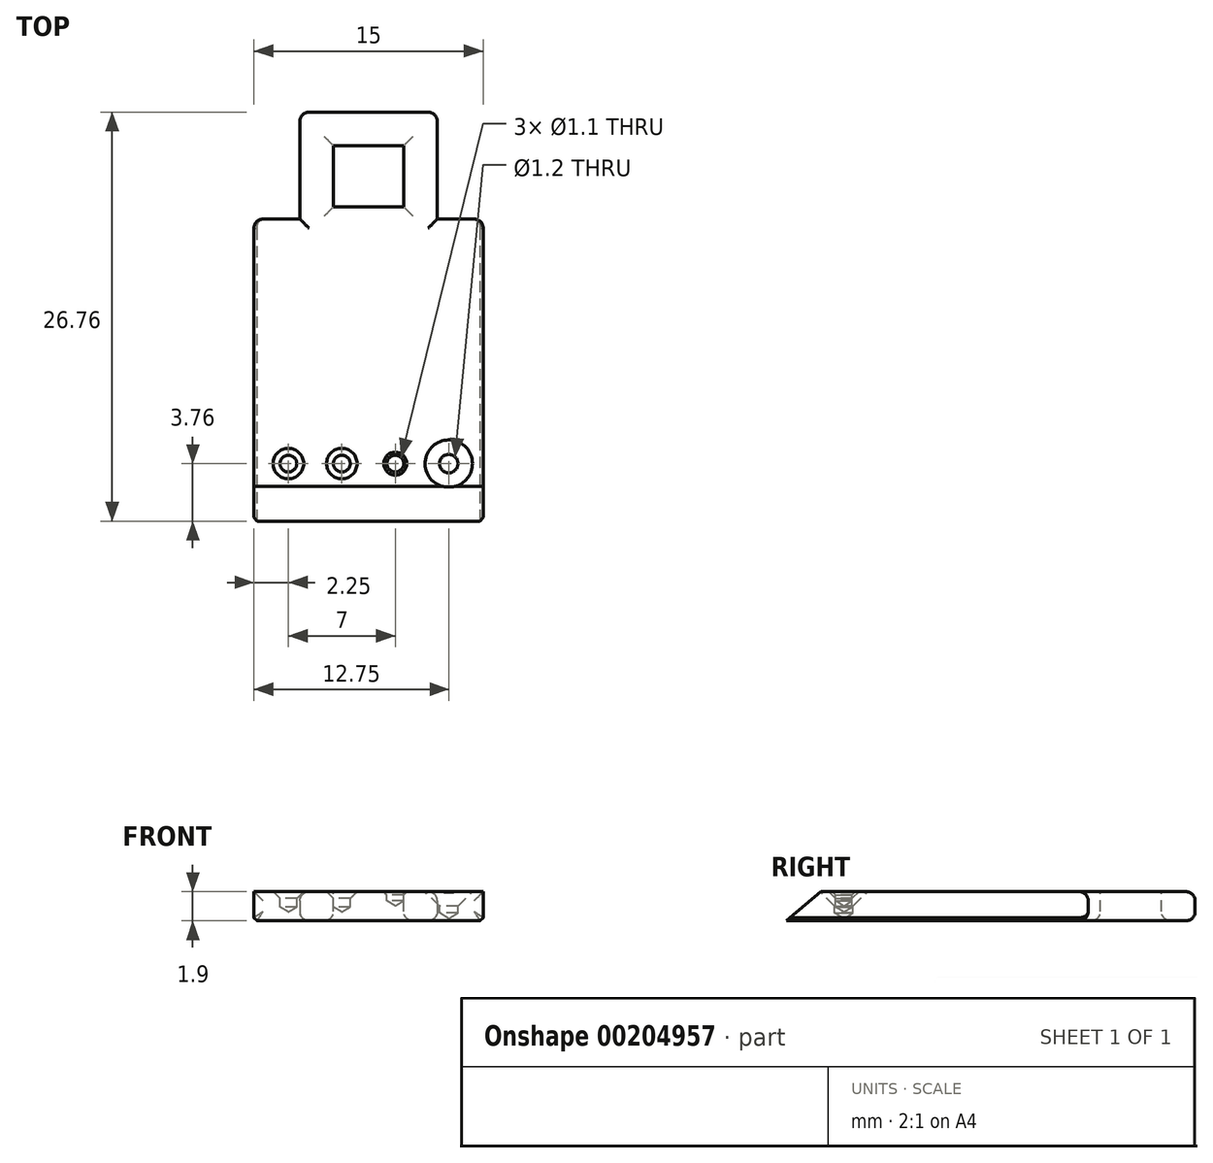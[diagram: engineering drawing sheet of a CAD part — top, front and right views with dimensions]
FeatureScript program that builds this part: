
annotation { "Feature Type Name" : "Feature", "Feature Type Description" : "" }
export const myFeature = defineFeature(function(context is Context, id is Id, definition is map)
    precondition{}
    {
        {
            var Q0;
            Q0=qCreatedBy(makeId("Top.planeOp"),FACE);
            var sketch = newSketch(context, id + "F0", { "sketchPlane" : qUnion([Q0])});
            skLineSegment(sketch, "E0.bottom", {"start": v(-7.5, 0) * mm, "end": v(7.5, 0) * mm});
            skLineSegment(sketch, "E0.top", {"start": v(-7.5, 20) * mm, "end": v(7.5, 20) * mm});
            skLineSegment(sketch, "E0.left", {"start": v(-7.5, 0) * mm, "end": v(-7.5, 20) * mm});
            skLineSegment(sketch, "E0.right", {"start": v(7.5, 0) * mm, "end": v(7.5, 20) * mm});
            skSolve(sketch);
        }
        {
            var Q0;
            Q0 = qSketchRegion(id + "F0", true);
            extrude(context, id + "F1", {"entities" : qUnion([Q0]), "depth" : 1.9 * mm});
        }
        {
            var Q0;
            Q0=makeQuery(id+"F1.opExtrude","CAP_FACE",FACE,{"disambiguationData":[OSD([sQuery(id+"F0.wireOp",EDGE,"E0.bottom"),sQuery(id+"F0.wireOp",EDGE,"E0.top"),sQuery(id+"F0.wireOp",EDGE,"E0.left"),sQuery(id+"F0.wireOp",EDGE,"E0.right")])],"isStart":false});
            var sketch = newSketch(context, id + "F2", { "sketchPlane" : qUnion([Q0])});
            skLineSegment(sketch, "E1", {"start": v(-7.5, 4) * mm, "end": v(7.5, 4) * mm, "construction": true});
            skPoint(sketch, "E2", {"position": v(-5.25, 4) * mm});
            skPoint(sketch, "E3", {"position": v(-1.75, 4) * mm});
            skPoint(sketch, "E4", {"position": v(1.75, 4) * mm});
            skPoint(sketch, "E5", {"position": v(5.25, 4) * mm});
            skSolve(sketch);
        }
        {
            var Q0;
            Q0=sQuery(id+"F2.wireOp",VERTEX,"E2");
            var Q1;
            Q1=sQuery(id+"F2.wireOp",VERTEX,"E3");
            var Q2;
            Q2=makeQuery(id+"F1.opExtrude","SWEPT_BODY",BODY,{"disambiguationData":[OSD([sQuery(id+"F0.wireOp",EDGE,"E0.bottom"),sQuery(id+"F0.wireOp",EDGE,"E0.top"),sQuery(id+"F0.wireOp",EDGE,"E0.left"),sQuery(id+"F0.wireOp",EDGE,"E0.right")])]});
            hole(context, id + "F3", {"style" : HoleStyle.C_SINK, "endStyle" : HoleEndStyle.BLIND, "holeDiameter" : 1.1 * mm, "cSinkDiameter" : 2 * mm, "cSinkAngle" : 90 * degree, "holeDepth" : 1 * mm, "locations" : qUnion([Q0, Q1]), "scope" : qUnion([Q2])});
        }
        {
            var Q0;
            Q0=sQuery(id+"F2.wireOp",VERTEX,"E4");
            var Q1;
            Q1=makeQuery(id+"F1.opExtrude","SWEPT_BODY",BODY,{"disambiguationData":[OSD([sQuery(id+"F0.wireOp",EDGE,"E0.bottom"),sQuery(id+"F0.wireOp",EDGE,"E0.top"),sQuery(id+"F0.wireOp",EDGE,"E0.left"),sQuery(id+"F0.wireOp",EDGE,"E0.right")])]});
            hole(context, id + "F4", {"style" : HoleStyle.C_SINK, "endStyle" : HoleEndStyle.BLIND, "holeDiameter" : 1.1 * mm, "cSinkDiameter" : 1.5 * mm, "cSinkAngle" : 90 * degree, "holeDepth" : .6 * mm, "locations" : qUnion([Q0]), "scope" : qUnion([Q1])});
        }
        {
            var Q0;
            Q0=sQuery(id+"F2.wireOp",VERTEX,"E5");
            var Q1;
            Q1=makeQuery(id+"F1.opExtrude","SWEPT_BODY",BODY,{"disambiguationData":[OSD([sQuery(id+"F0.wireOp",EDGE,"E0.bottom"),sQuery(id+"F0.wireOp",EDGE,"E0.top"),sQuery(id+"F0.wireOp",EDGE,"E0.left"),sQuery(id+"F0.wireOp",EDGE,"E0.right")])]});
            hole(context, id + "F5", {"style" : HoleStyle.C_SINK, "endStyle" : HoleEndStyle.BLIND, "holeDiameter" : 1.2 * mm, "cSinkDiameter" : 3.1 * mm, "cSinkAngle" : 90 * degree, "holeDepth" : 1.4 * mm, "locations" : qUnion([Q0]), "scope" : qUnion([Q1])});
        }
        {
            var Q0;
            Q0=makeQuery(id+"F1.opExtrude","CAP_EDGE",EDGE,{"disambiguationData":[OSD([sQuery(id+"F0.wireOp",EDGE,"E0.bottom")])],"isStart":false});
            chamfer(context, id + "F6", {"entities" : qUnion([Q0]), "chamferType" : ChamferType.OFFSET_ANGLE, "width" : 2.5 * mm, "oppositeDirection" : false, "angle" : 40 * degree, "tangentPropagation" : true});
        }
        {
            var Q0;
            Q0=makeQuery(id+"F1.opExtrude","SWEPT_FACE",FACE,{"disambiguationData":[OSD([sQuery(id+"F0.wireOp",EDGE,"E0.top")])]});
            var sketch = newSketch(context, id + "F7", { "sketchPlane" : qUnion([Q0])});
            skLineSegment(sketch, "E6.bottom", {"start": v(-4.5, 1.9) * mm, "end": v(4.5, 1.9) * mm});
            skLineSegment(sketch, "E6.top", {"start": v(-4.5, 0) * mm, "end": v(4.5, 0) * mm});
            skLineSegment(sketch, "E6.left", {"start": v(-4.5, 1.9) * mm, "end": v(-4.5, 0) * mm});
            skLineSegment(sketch, "E6.right", {"start": v(4.5, 1.9) * mm, "end": v(4.5, 0) * mm});
            skSolve(sketch);
        }
        {
            var Q0;
            Q0 = qSketchRegion(id + "F7", true);
            extrude(context, id + "F8", {"entities" : qUnion([Q0]), "operationType" : NewBodyOperationType.ADD, "depth" : 7 * mm});
        }
        {
            var Q0;
            Q0=makeQuery(id+"F8.boolean.opBoolean","MERGE",FACE,{"derivedFrom":[makeQuery(id+"F1.opExtrude","CAP_FACE",FACE,{"disambiguationData":[OSD([sQuery(id+"F0.wireOp",EDGE,"E0.bottom"),sQuery(id+"F0.wireOp",EDGE,"E0.top"),sQuery(id+"F0.wireOp",EDGE,"E0.left"),sQuery(id+"F0.wireOp",EDGE,"E0.right")])],"isStart":false}),makeQuery(id+"F8.opExtrude","SWEPT_FACE",FACE,{"disambiguationData":[OSD([sQuery(id+"F7.wireOp",EDGE,"E6.bottom")])]})]});
            var sketch = newSketch(context, id + "F9", { "sketchPlane" : qUnion([Q0])});
            skLineSegment(sketch, "E7.bottom", {"start": v(-2.3, 24.8) * mm, "end": v(2.3, 24.8) * mm});
            skLineSegment(sketch, "E7.top", {"start": v(-2.3, 20.8) * mm, "end": v(2.3, 20.8) * mm});
            skLineSegment(sketch, "E7.left", {"start": v(-2.3, 24.8) * mm, "end": v(-2.3, 20.8) * mm});
            skLineSegment(sketch, "E7.right", {"start": v(2.3, 24.8) * mm, "end": v(2.3, 20.8) * mm});
            skSolve(sketch);
        }
        {
            var Q0;
            Q0 = qSketchRegion(id + "F9", true);
            extrude(context, id + "F10", {"entities" : qUnion([Q0]), "operationType" : NewBodyOperationType.REMOVE, "oppositeDirection" : true, "depth" : 25 * mm});
        }
        {
            var Q0;
            Q0=makeQuery(id+"F10.boolean.opBoolean","COPY",EDGE,{"derivedFrom":makeQuery(id+"F10.opExtrude","CAP_EDGE",EDGE,{"disambiguationData":[OSD([sQuery(id+"F9.wireOp",EDGE,"E7.left")])],"isStart":true})});
            var Q1;
            Q1=makeQuery(id+"F10.boolean.opBoolean","COPY",EDGE,{"derivedFrom":makeQuery(id+"F10.opExtrude","CAP_EDGE",EDGE,{"disambiguationData":[OSD([sQuery(id+"F9.wireOp",EDGE,"E7.bottom")])],"isStart":true})});
            var Q2;
            Q2=makeQuery(id+"F10.boolean.opBoolean","COPY",EDGE,{"derivedFrom":makeQuery(id+"F10.opExtrude","CAP_EDGE",EDGE,{"disambiguationData":[OSD([sQuery(id+"F9.wireOp",EDGE,"E7.right")])],"isStart":true})});
            var Q3;
            Q3=makeQuery(id+"F10.boolean.opBoolean","COPY",EDGE,{"derivedFrom":makeQuery(id+"F10.opExtrude","CAP_EDGE",EDGE,{"disambiguationData":[OSD([sQuery(id+"F9.wireOp",EDGE,"E7.top")])],"isStart":true})});
            var Q4;
            Q4=makeQuery(id+"F8.opExtrude","CAP_EDGE",EDGE,{"disambiguationData":[OSD([sQuery(id+"F7.wireOp",EDGE,"E6.bottom")])],"isStart":false});
            var Q5;
            Q5=makeQuery(id+"F8.opExtrude","SWEPT_EDGE",EDGE,{"disambiguationData":[OSD([sQuery(id+"F0.wireOp",EDGE,"E0.top"),sQuery(id+"F7.wireOp",EDGE,"E6.bottom"),sQuery(id+"F7.wireOp",EDGE,"E6.right")])]});
            var Q6;
            Q6=makeQuery(id+"F8.opExtrude","SWEPT_EDGE",EDGE,{"disambiguationData":[OSD([sQuery(id+"F0.wireOp",EDGE,"E0.top"),sQuery(id+"F7.wireOp",EDGE,"E6.bottom"),sQuery(id+"F7.wireOp",EDGE,"E6.left")])]});
            var Q7;
            {var subQ0=sQuery(id+"F0.wireOp",EDGE,"E0.right");var subQ1=sQuery(id+"F0.wireOp",EDGE,"E0.top");Q7=makeQuery(id+"F8.boolean.opBoolean","SPLIT",EDGE,{"disambiguationData":[TD([makeQuery(id+"F1.opExtrude","SWEPT_FACE",FACE,{"disambiguationData":[OSD([subQ0])]})])],"derivedFrom":makeQuery(id+"F1.opExtrude","CAP_EDGE",EDGE,{"disambiguationData":[OSD([subQ1])],"isStart":false})});}
            var Q8;
            {var subQ0=sQuery(id+"F0.wireOp",EDGE,"E0.left");var subQ1=sQuery(id+"F0.wireOp",EDGE,"E0.top");Q8=makeQuery(id+"F8.boolean.opBoolean","SPLIT",EDGE,{"disambiguationData":[TD([makeQuery(id+"F1.opExtrude","SWEPT_FACE",FACE,{"disambiguationData":[OSD([subQ0])]})])],"derivedFrom":makeQuery(id+"F1.opExtrude","CAP_EDGE",EDGE,{"disambiguationData":[OSD([subQ1])],"isStart":false})});}
            var Q9;
            Q9=makeQuery(id+"F1.opExtrude","SWEPT_EDGE",EDGE,{"disambiguationData":[OSD([sQuery(id+"F0.wireOp",EDGE,"E0.top"),sQuery(id+"F0.wireOp",EDGE,"E0.left")])]});
            var Q10;
            {var subQ0=sQuery(id+"F0.wireOp",EDGE,"E0.left");var subQ1=sQuery(id+"F0.wireOp",EDGE,"E0.top");Q10=makeQuery(id+"F8.boolean.opBoolean","SPLIT",EDGE,{"disambiguationData":[TD([makeQuery(id+"F1.opExtrude","SWEPT_FACE",FACE,{"disambiguationData":[OSD([subQ0])]})])],"derivedFrom":makeQuery(id+"F1.opExtrude","CAP_EDGE",EDGE,{"disambiguationData":[OSD([subQ1])],"isStart":true})});}
            var Q11;
            Q11=makeQuery(id+"F8.opExtrude","SWEPT_EDGE",EDGE,{"disambiguationData":[OSD([sQuery(id+"F0.wireOp",EDGE,"E0.top"),sQuery(id+"F7.wireOp",EDGE,"E6.top"),sQuery(id+"F7.wireOp",EDGE,"E6.right")])]});
            var Q12;
            Q12=makeQuery(id+"F8.opExtrude","CAP_EDGE",EDGE,{"disambiguationData":[OSD([sQuery(id+"F7.wireOp",EDGE,"E6.top")])],"isStart":false});
            var Q13;
            Q13=makeQuery(id+"F10.boolean.opBoolean","INTERSECT",EDGE,{"derivedFrom":[makeQuery(id+"F8.boolean.opBoolean","MERGE",FACE,{"derivedFrom":[makeQuery(id+"F1.opExtrude","CAP_FACE",FACE,{"disambiguationData":[OSD([sQuery(id+"F0.wireOp",EDGE,"E0.bottom"),sQuery(id+"F0.wireOp",EDGE,"E0.top"),sQuery(id+"F0.wireOp",EDGE,"E0.left"),sQuery(id+"F0.wireOp",EDGE,"E0.right")])],"isStart":true}),makeQuery(id+"F8.opExtrude","SWEPT_FACE",FACE,{"disambiguationData":[OSD([sQuery(id+"F7.wireOp",EDGE,"E6.top")])]})]}),makeQuery(id+"F10.opExtrude","SWEPT_FACE",FACE,{"disambiguationData":[OSD([sQuery(id+"F9.wireOp",EDGE,"E7.top")])]})]});
            var Q14;
            Q14=makeQuery(id+"F10.boolean.opBoolean","INTERSECT",EDGE,{"derivedFrom":[makeQuery(id+"F8.boolean.opBoolean","MERGE",FACE,{"derivedFrom":[makeQuery(id+"F1.opExtrude","CAP_FACE",FACE,{"disambiguationData":[OSD([sQuery(id+"F0.wireOp",EDGE,"E0.bottom"),sQuery(id+"F0.wireOp",EDGE,"E0.top"),sQuery(id+"F0.wireOp",EDGE,"E0.left"),sQuery(id+"F0.wireOp",EDGE,"E0.right")])],"isStart":true}),makeQuery(id+"F8.opExtrude","SWEPT_FACE",FACE,{"disambiguationData":[OSD([sQuery(id+"F7.wireOp",EDGE,"E6.top")])]})]}),makeQuery(id+"F10.opExtrude","SWEPT_FACE",FACE,{"disambiguationData":[OSD([sQuery(id+"F9.wireOp",EDGE,"E7.left")])]})]});
            var Q15;
            Q15=makeQuery(id+"F10.boolean.opBoolean","INTERSECT",EDGE,{"derivedFrom":[makeQuery(id+"F8.boolean.opBoolean","MERGE",FACE,{"derivedFrom":[makeQuery(id+"F1.opExtrude","CAP_FACE",FACE,{"disambiguationData":[OSD([sQuery(id+"F0.wireOp",EDGE,"E0.bottom"),sQuery(id+"F0.wireOp",EDGE,"E0.top"),sQuery(id+"F0.wireOp",EDGE,"E0.left"),sQuery(id+"F0.wireOp",EDGE,"E0.right")])],"isStart":true}),makeQuery(id+"F8.opExtrude","SWEPT_FACE",FACE,{"disambiguationData":[OSD([sQuery(id+"F7.wireOp",EDGE,"E6.top")])]})]}),makeQuery(id+"F10.opExtrude","SWEPT_FACE",FACE,{"disambiguationData":[OSD([sQuery(id+"F9.wireOp",EDGE,"E7.bottom")])]})]});
            var Q16;
            Q16=makeQuery(id+"F10.boolean.opBoolean","INTERSECT",EDGE,{"derivedFrom":[makeQuery(id+"F8.boolean.opBoolean","MERGE",FACE,{"derivedFrom":[makeQuery(id+"F1.opExtrude","CAP_FACE",FACE,{"disambiguationData":[OSD([sQuery(id+"F0.wireOp",EDGE,"E0.bottom"),sQuery(id+"F0.wireOp",EDGE,"E0.top"),sQuery(id+"F0.wireOp",EDGE,"E0.left"),sQuery(id+"F0.wireOp",EDGE,"E0.right")])],"isStart":true}),makeQuery(id+"F8.opExtrude","SWEPT_FACE",FACE,{"disambiguationData":[OSD([sQuery(id+"F7.wireOp",EDGE,"E6.top")])]})]}),makeQuery(id+"F10.opExtrude","SWEPT_FACE",FACE,{"disambiguationData":[OSD([sQuery(id+"F9.wireOp",EDGE,"E7.right")])]})]});
            var Q17;
            Q17=makeQuery(id+"F8.opExtrude","SWEPT_EDGE",EDGE,{"disambiguationData":[OSD([sQuery(id+"F0.wireOp",EDGE,"E0.top"),sQuery(id+"F7.wireOp",EDGE,"E6.top"),sQuery(id+"F7.wireOp",EDGE,"E6.left")])]});
            var Q18;
            {var subQ0=sQuery(id+"F0.wireOp",EDGE,"E0.right");var subQ1=sQuery(id+"F0.wireOp",EDGE,"E0.top");Q18=makeQuery(id+"F8.boolean.opBoolean","SPLIT",EDGE,{"disambiguationData":[TD([makeQuery(id+"F1.opExtrude","SWEPT_FACE",FACE,{"disambiguationData":[OSD([subQ0])]})])],"derivedFrom":makeQuery(id+"F1.opExtrude","CAP_EDGE",EDGE,{"disambiguationData":[OSD([subQ1])],"isStart":true})});}
            var Q19;
            Q19=makeQuery(id+"F1.opExtrude","SWEPT_EDGE",EDGE,{"disambiguationData":[OSD([sQuery(id+"F0.wireOp",EDGE,"E0.top"),sQuery(id+"F0.wireOp",EDGE,"E0.right")])]});
            var Q20;
            Q20=makeQuery(id+"F8.opExtrude","CAP_EDGE",EDGE,{"disambiguationData":[OSD([sQuery(id+"F7.wireOp",EDGE,"E6.left")])],"isStart":false});
            var Q21;
            Q21=makeQuery(id+"F8.opExtrude","CAP_EDGE",EDGE,{"disambiguationData":[OSD([sQuery(id+"F7.wireOp",EDGE,"E6.right")])],"isStart":false});
            fillet(context, id + "F11", {"entities" : qUnion([Q0, Q1, Q2, Q3, Q4, Q5, Q6, Q7, Q8, Q9, Q10, Q11, Q12, Q13, Q14, Q15, Q16, Q17, Q18, Q19, Q20, Q21]), "radius" : .6 * mm, "tangentPropagation" : true, "allowEdgeOverflow" : false});
        }
        {
            var Q0;
            Q0=makeQuery(id+"F1.opExtrude","CAP_EDGE",EDGE,{"disambiguationData":[OSD([sQuery(id+"F0.wireOp",EDGE,"E0.left")])],"isStart":true});
            var Q1;
            Q1=makeQuery(id+"F1.opExtrude","CAP_EDGE",EDGE,{"disambiguationData":[OSD([sQuery(id+"F0.wireOp",EDGE,"E0.right")])],"isStart":true});
            chamfer(context, id + "F12", {"entities" : qUnion([Q0, Q1]), "width" : .2 * mm, "tangentPropagation" : true});
        }
    });
